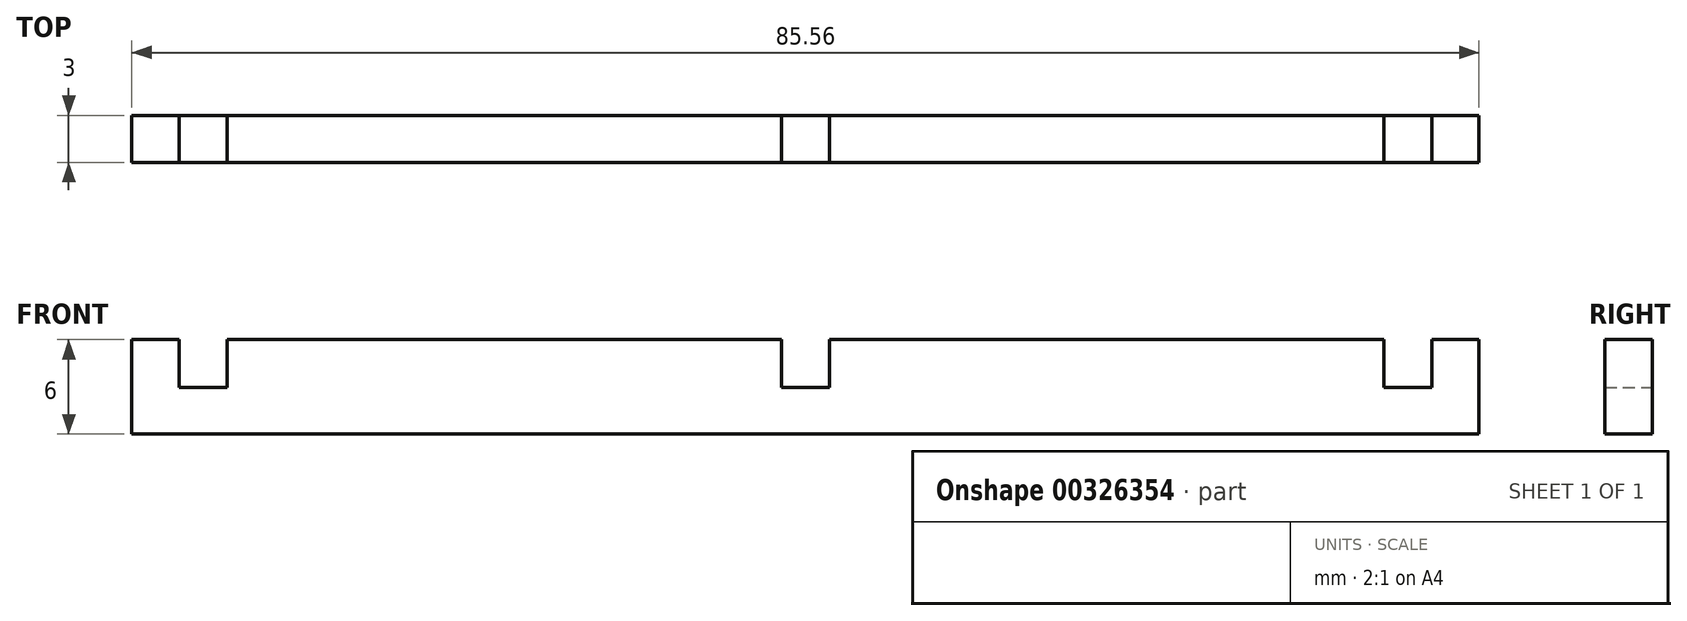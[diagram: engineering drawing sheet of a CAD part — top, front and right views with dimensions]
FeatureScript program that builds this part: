
annotation { "Feature Type Name" : "Feature", "Feature Type Description" : "" }
export const myFeature = defineFeature(function(context is Context, id is Id, definition is map)
    precondition{}
    {
        {
            var Q0;
            Q0=qCreatedBy(makeId("Front.planeOp"),FACE);
            var sketch = newSketch(context, id + "F0", { "sketchPlane" : qUnion([Q0])});
            skLineSegment(sketch, "E0", {"start": v(-42.78, -3.23) * mm, "end": v(-42.78, 2.77) * mm});
            skLineSegment(sketch, "E1", {"start": v(-42.78, 2.77) * mm, "end": v(-39.78, 2.77) * mm});
            skLineSegment(sketch, "E2", {"start": v(42.78, 2.77) * mm, "end": v(42.78, -3.23) * mm});
            skPoint(sketch, "E3", {"position": v(-39.78, -0.25) * mm});
            skPoint(sketch, "E4", {"position": v(-36.74, -0.25) * mm});
            skPoint(sketch, "E5", {"position": v(39.78, -0.25) * mm});
            skPoint(sketch, "E6", {"position": v(36.74, -0.25) * mm});
            skLineSegment(sketch, "E7", {"start": v(-36.74, -0.25) * mm, "end": v(-39.78, -0.25) * mm});
            skLineSegment(sketch, "E8", {"start": v(39.78, -0.25) * mm, "end": v(36.74, -0.25) * mm});
            skLineSegment(sketch, "E9", {"start": v(-42.78, -3.23) * mm, "end": v(42.78, -3.23) * mm});
            skLineSegment(sketch, "E10", {"start": v(39.78, -0.25) * mm, "end": v(39.78, 2.77) * mm});
            skLineSegment(sketch, "E11", {"start": v(36.74, -0.25) * mm, "end": v(36.74, 2.77) * mm});
            skLineSegment(sketch, "E12", {"start": v(-39.78, -0.25) * mm, "end": v(-39.78, 2.77) * mm});
            skLineSegment(sketch, "E13", {"start": v(-36.74, -0.25) * mm, "end": v(-36.74, 2.77) * mm});
            skLineSegment(sketch, "E14.trimOffspring", {"start": v(-36.74, 2.77) * mm, "end": v(-1.52, 2.77) * mm});
            skLineSegment(sketch, "E15.trimOffspring", {"start": v(39.78, 2.77) * mm, "end": v(42.78, 2.77) * mm});
            skLineSegment(sketch, "E16", {"start": v(-1.52, 2.77) * mm, "end": v(-1.52, -0.25) * mm});
            skLineSegment(sketch, "E17", {"start": v(-1.52, -0.25) * mm, "end": v(1.52, -0.25) * mm});
            skLineSegment(sketch, "E18", {"start": v(1.52, -0.25) * mm, "end": v(1.52, 2.77) * mm});
            skLineSegment(sketch, "E19.trimOffspring", {"start": v(1.52, 2.77) * mm, "end": v(36.74, 2.77) * mm});
            skSolve(sketch);
        }
        {
            var Q0;
            Q0=makeQuery(id+"F0.imprint","IMPRINT",FACE,{"disambiguationData":[TD([[makeQuery(id+"F0.imprint","IMPRINT",EDGE,{"derivedFrom":sQuery(id+"F0.wireOp",EDGE,"E0")}),-1.0]])]});
            extrude(context, id + "F1", {"entities" : qUnion([Q0]), "depth" : 3 * mm});
        }
    });
